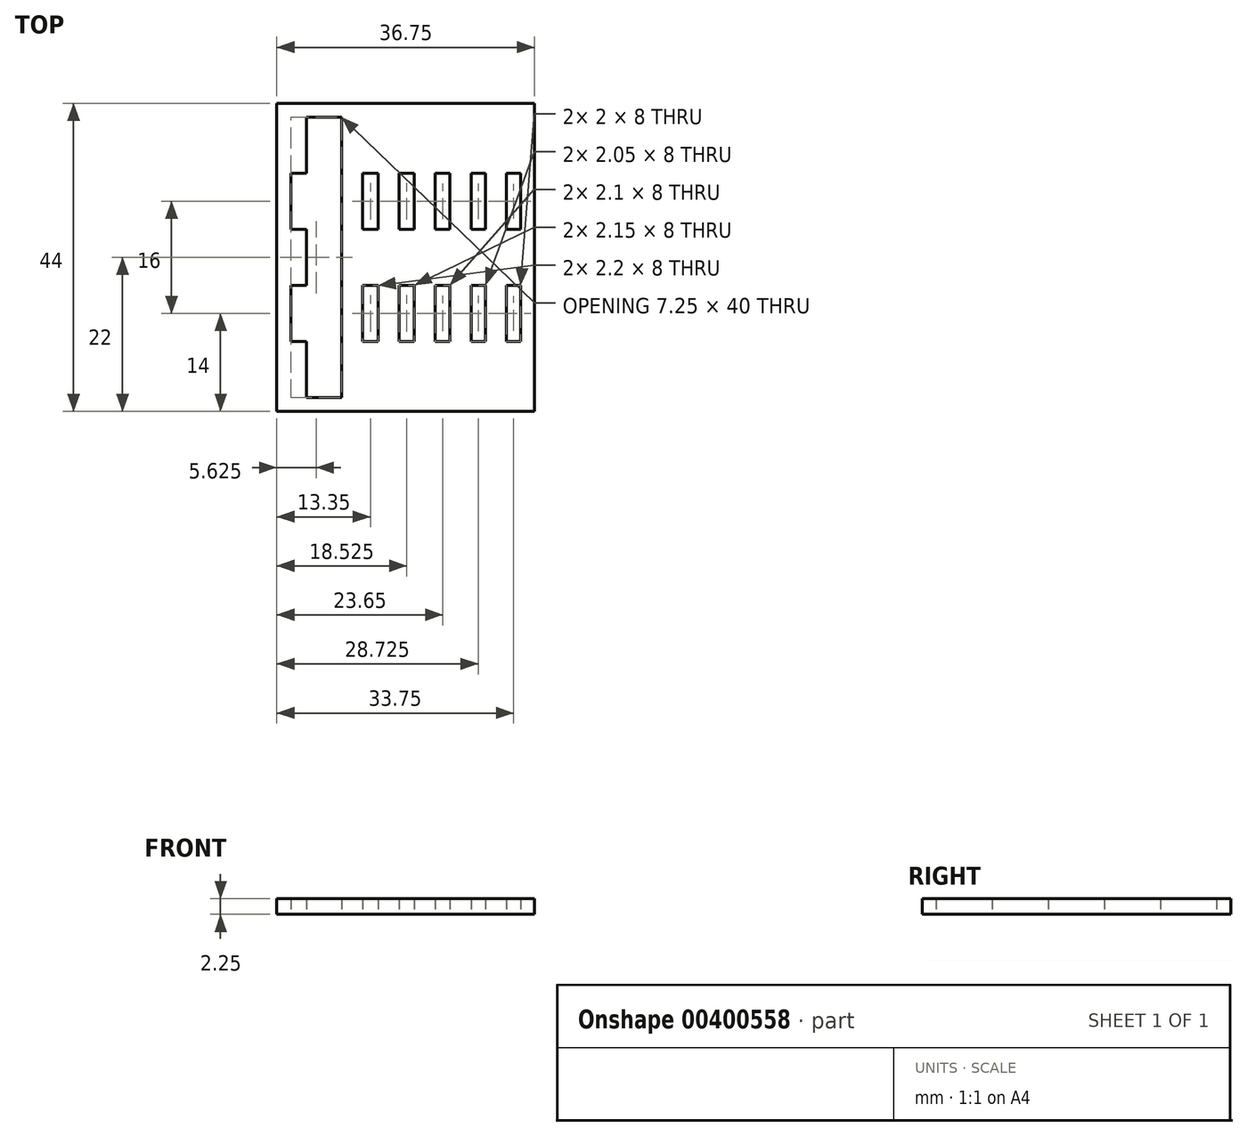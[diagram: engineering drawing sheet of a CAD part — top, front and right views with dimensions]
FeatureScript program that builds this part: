
annotation { "Feature Type Name" : "Feature", "Feature Type Description" : "" }
export const myFeature = defineFeature(function(context is Context, id is Id, definition is map)
    precondition{}
    {
        {
            var Q0;
            Q0=qCreatedBy(makeId("Top.planeOp"),FACE);
            var sketch = newSketch(context, id + "F0", { "sketchPlane" : qUnion([Q0])});
            skLineSegment(sketch, "E0.bottom", {"start": v(0, 44) * mm, "end": v(36.75, 44) * mm});
            skLineSegment(sketch, "E0.top", {"start": v(0, 0) * mm, "end": v(36.75, 0) * mm});
            skLineSegment(sketch, "E0.left", {"start": v(0, 44) * mm, "end": v(0, 0) * mm});
            skLineSegment(sketch, "E0.right", {"start": v(36.75, 44) * mm, "end": v(36.75, 0) * mm});
            skLineSegment(sketch, "E1", {"start": v(4.25, 2) * mm, "end": v(4.25, 10) * mm});
            skLineSegment(sketch, "E2", {"start": v(4.25, 10) * mm, "end": v(2, 10) * mm});
            skLineSegment(sketch, "E3", {"start": v(2, 10) * mm, "end": v(2, 18) * mm});
            skLineSegment(sketch, "E4", {"start": v(2, 18) * mm, "end": v(4.25, 18) * mm});
            skLineSegment(sketch, "E5", {"start": v(4.25, 18) * mm, "end": v(4.25, 26) * mm});
            skLineSegment(sketch, "E6", {"start": v(4.25, 26) * mm, "end": v(2, 26) * mm});
            skLineSegment(sketch, "E7", {"start": v(2, 26) * mm, "end": v(2, 34) * mm});
            skLineSegment(sketch, "E8", {"start": v(2, 34) * mm, "end": v(4.25, 34) * mm});
            skLineSegment(sketch, "E9", {"start": v(4.25, 34) * mm, "end": v(4.25, 42) * mm});
            skLineSegment(sketch, "E10", {"start": v(4.25, 42) * mm, "end": v(9.25, 42) * mm});
            skLineSegment(sketch, "E11", {"start": v(9.25, 42) * mm, "end": v(9.25, 2) * mm});
            skLineSegment(sketch, "E12", {"start": v(9.25, 2) * mm, "end": v(4.25, 2) * mm});
            skLineSegment(sketch, "E13.bottom", {"start": v(12.25, 34) * mm, "end": v(14.45, 34) * mm});
            skLineSegment(sketch, "E13.top", {"start": v(12.25, 26) * mm, "end": v(14.45, 26) * mm});
            skLineSegment(sketch, "E13.left", {"start": v(12.25, 34) * mm, "end": v(12.25, 26) * mm});
            skLineSegment(sketch, "E13.right", {"start": v(14.45, 34) * mm, "end": v(14.45, 26) * mm});
            skLineSegment(sketch, "E14.bottom", {"start": v(12.25, 18) * mm, "end": v(14.45, 18) * mm});
            skLineSegment(sketch, "E14.top", {"start": v(12.25, 10) * mm, "end": v(14.45, 10) * mm});
            skLineSegment(sketch, "E14.left", {"start": v(12.25, 18) * mm, "end": v(12.25, 10) * mm});
            skLineSegment(sketch, "E14.right", {"start": v(14.45, 18) * mm, "end": v(14.45, 10) * mm});
            skLineSegment(sketch, "E15.bottom", {"start": v(17.45, 34) * mm, "end": v(19.6, 34) * mm});
            skLineSegment(sketch, "E15.top", {"start": v(17.45, 26) * mm, "end": v(19.6, 26) * mm});
            skLineSegment(sketch, "E15.left", {"start": v(17.45, 34) * mm, "end": v(17.45, 26) * mm});
            skLineSegment(sketch, "E15.right", {"start": v(19.6, 34) * mm, "end": v(19.6, 26) * mm});
            skLineSegment(sketch, "E16.bottom", {"start": v(17.45, 18) * mm, "end": v(19.6, 18) * mm});
            skLineSegment(sketch, "E16.top", {"start": v(17.45, 10) * mm, "end": v(19.6, 10) * mm});
            skLineSegment(sketch, "E16.left", {"start": v(17.45, 18) * mm, "end": v(17.45, 10) * mm});
            skLineSegment(sketch, "E16.right", {"start": v(19.6, 18) * mm, "end": v(19.6, 10) * mm});
            skLineSegment(sketch, "E17.bottom", {"start": v(22.6, 34) * mm, "end": v(24.7, 34) * mm});
            skLineSegment(sketch, "E17.top", {"start": v(22.6, 26) * mm, "end": v(24.7, 26) * mm});
            skLineSegment(sketch, "E17.left", {"start": v(22.6, 34) * mm, "end": v(22.6, 26) * mm});
            skLineSegment(sketch, "E17.right", {"start": v(24.7, 34) * mm, "end": v(24.7, 26) * mm});
            skLineSegment(sketch, "E18.bottom", {"start": v(22.6, 18) * mm, "end": v(24.7, 18) * mm});
            skLineSegment(sketch, "E18.top", {"start": v(22.6, 10) * mm, "end": v(24.7, 10) * mm});
            skLineSegment(sketch, "E18.left", {"start": v(22.6, 18) * mm, "end": v(22.6, 10) * mm});
            skLineSegment(sketch, "E18.right", {"start": v(24.7, 18) * mm, "end": v(24.7, 10) * mm});
            skLineSegment(sketch, "E19.bottom", {"start": v(27.7, 34) * mm, "end": v(29.75, 34) * mm});
            skLineSegment(sketch, "E19.top", {"start": v(27.7, 26) * mm, "end": v(29.75, 26) * mm});
            skLineSegment(sketch, "E19.left", {"start": v(27.7, 34) * mm, "end": v(27.7, 26) * mm});
            skLineSegment(sketch, "E19.right", {"start": v(29.75, 34) * mm, "end": v(29.75, 26) * mm});
            skLineSegment(sketch, "E20.bottom", {"start": v(27.7, 18) * mm, "end": v(29.75, 18) * mm});
            skLineSegment(sketch, "E20.top", {"start": v(27.7, 10) * mm, "end": v(29.75, 10) * mm});
            skLineSegment(sketch, "E20.left", {"start": v(27.7, 18) * mm, "end": v(27.7, 10) * mm});
            skLineSegment(sketch, "E20.right", {"start": v(29.75, 18) * mm, "end": v(29.75, 10) * mm});
            skLineSegment(sketch, "E21.bottom", {"start": v(32.75, 10) * mm, "end": v(34.75, 10) * mm});
            skLineSegment(sketch, "E21.top", {"start": v(32.75, 18) * mm, "end": v(34.75, 18) * mm});
            skLineSegment(sketch, "E21.left", {"start": v(32.75, 10) * mm, "end": v(32.75, 18) * mm});
            skLineSegment(sketch, "E21.right", {"start": v(34.75, 10) * mm, "end": v(34.75, 18) * mm});
            skLineSegment(sketch, "E22.bottom", {"start": v(32.75, 26) * mm, "end": v(34.75, 26) * mm});
            skLineSegment(sketch, "E22.top", {"start": v(32.75, 34) * mm, "end": v(34.75, 34) * mm});
            skLineSegment(sketch, "E22.left", {"start": v(32.75, 26) * mm, "end": v(32.75, 34) * mm});
            skLineSegment(sketch, "E22.right", {"start": v(34.75, 26) * mm, "end": v(34.75, 34) * mm});
            skSolve(sketch);
        }
        {
            var Q0;
            Q0=makeQuery(id+"F0.imprint","IMPRINT",FACE,{"disambiguationData":[TD([[makeQuery(id+"F0.imprint","IMPRINT",EDGE,{"derivedFrom":sQuery(id+"F0.wireOp",EDGE,"E0.bottom")}),-1.0]])]});
            extrude(context, id + "F1", {"entities" : qUnion([Q0]), "depth" : 2.25 * mm});
        }
    });
